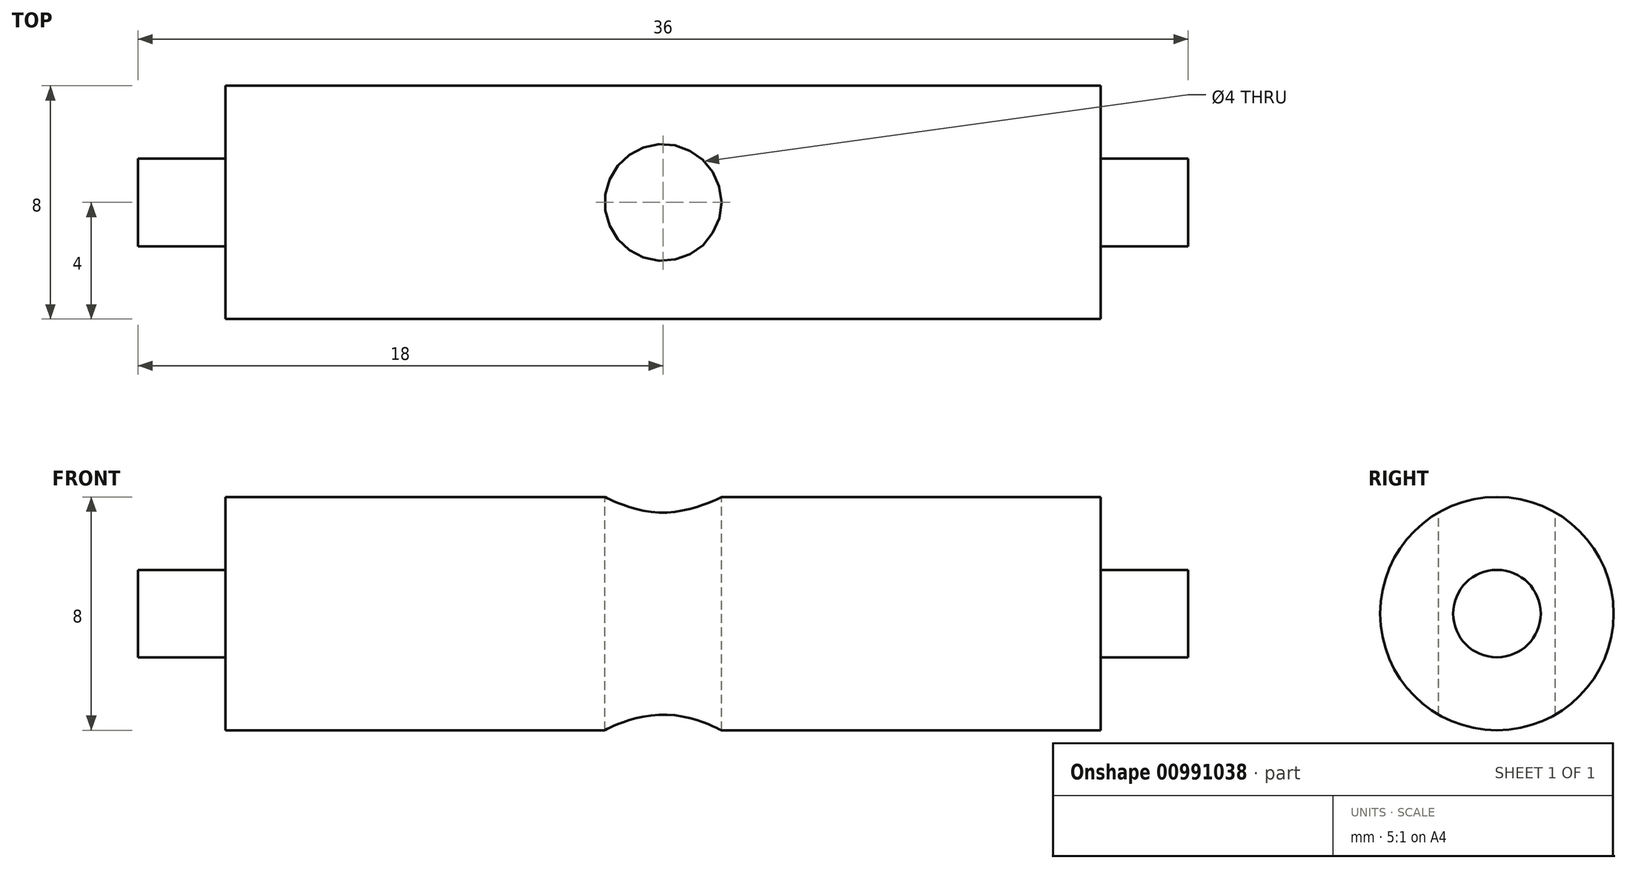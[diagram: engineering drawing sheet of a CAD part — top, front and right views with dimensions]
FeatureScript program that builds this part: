
annotation { "Feature Type Name" : "Feature", "Feature Type Description" : "" }
export const myFeature = defineFeature(function(context is Context, id is Id, definition is map)
    precondition{}
    {
        {
            var Q0;
            Q0=qCreatedBy(makeId("Top.planeOp"),FACE);
            var sketch = newSketch(context, id + "F0", { "sketchPlane" : qUnion([Q0])});
            skLineSegment(sketch, "E0", {"start": v(-36.1, 0) * mm, "end": v(43.6, 0) * mm, "construction": true});
            skLineSegment(sketch, "E1", {"start": v(-18, 0) * mm, "end": v(-18, 1.5) * mm});
            skLineSegment(sketch, "E2", {"start": v(-18, 1.5) * mm, "end": v(-15, 1.5) * mm});
            skLineSegment(sketch, "E3", {"start": v(-15, 1.5) * mm, "end": v(-15, 4) * mm});
            skLineSegment(sketch, "E4", {"start": v(-15, 4) * mm, "end": v(15, 4) * mm});
            skLineSegment(sketch, "E5", {"start": v(15, 4) * mm, "end": v(15, 1.5) * mm});
            skLineSegment(sketch, "E6", {"start": v(15, 1.5) * mm, "end": v(18, 1.5) * mm});
            skLineSegment(sketch, "E7", {"start": v(18, 1.5) * mm, "end": v(18, 0) * mm});
            skLineSegment(sketch, "E8", {"start": v(18, 0) * mm, "end": v(-18, 0) * mm});
            skSolve(sketch);
        }
        {
            var Q0;
            Q0=makeQuery(id+"F0.imprint","IMPRINT",FACE,{"disambiguationData":[TD([[makeQuery(id+"F0.imprint","IMPRINT",EDGE,{"derivedFrom":sQuery(id+"F0.wireOp",EDGE,"E1")}),-1.0]])]});
            var Q1;
            Q1=sQuery(id+"F0.wireOp",EDGE,"E8");
            revolve(context, id + "F1", {"surfaceOperationType" : NewSurfaceOperationType.NEW, "entities" : qUnion([Q0]), "axis" : qUnion([Q1]), "revolveType" : RevolveType.FULL});
        }
        {
            var Q0;
            Q0=qCreatedBy(makeId("Top.planeOp"),FACE);
            var sketch = newSketch(context, id + "F2", { "sketchPlane" : qUnion([Q0])});
            skCircle(sketch, "E9", {"center": v(0, 0) * mm, "radius": 2 * mm});
            skSolve(sketch);
        }
        {
            var Q0;
            Q0 = qSketchRegion(id + "F2", true);
            var Q1;
            Q1=sQuery(id+"Fw2oxCnPlJrZ6VZ_1.wireOp",EDGE,"XHLxiE9e-7D83-oT6u-JQhb-HBlY4MAKewRA");
            extrude(context, id + "F3", {"entities" : qUnion([Q0]), "operationType" : NewBodyOperationType.REMOVE, "surfaceEntities" : qUnion([Q1]), "endBound" : BoundingType.SYMMETRIC, "oppositeDirection" : true, "depth" : 10 * mm, "offsetDistance" : 25 * mm});
        }
    });
